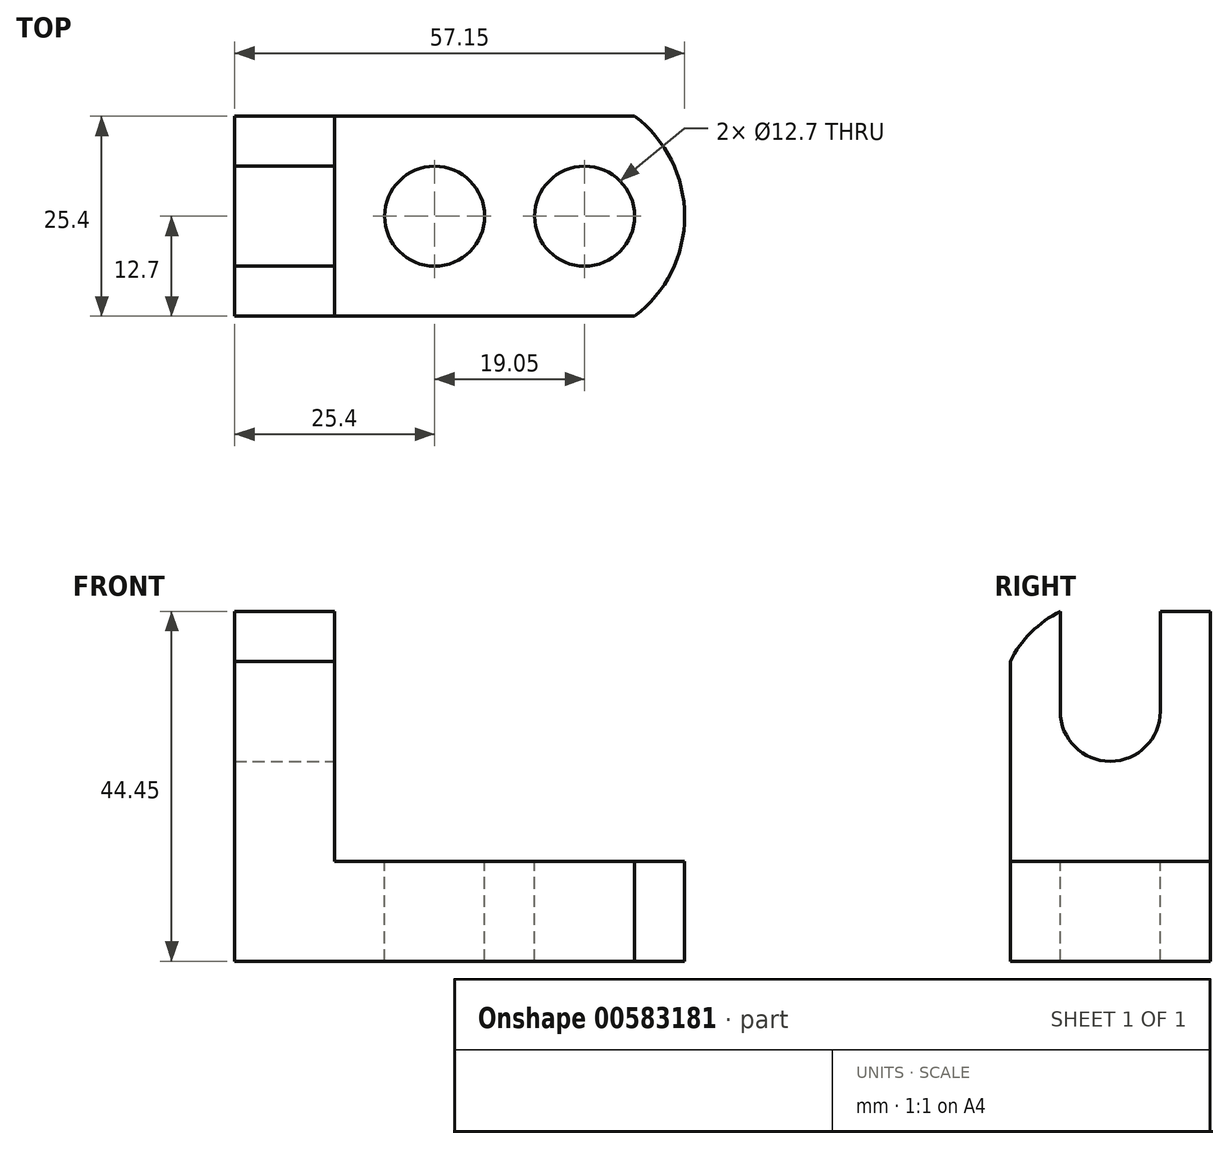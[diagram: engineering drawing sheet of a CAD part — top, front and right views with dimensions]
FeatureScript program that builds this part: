
annotation { "Feature Type Name" : "Feature", "Feature Type Description" : "" }
export const myFeature = defineFeature(function(context is Context, id is Id, definition is map)
    precondition{}
    {
        {
            var Q0;
            Q0=qCreatedBy(makeId("Front.planeOp"),FACE);
            var sketch = newSketch(context, id + "F0", { "sketchPlane" : qUnion([Q0])});
            skLineSegment(sketch, "E0.bottom", {"start": v(0, 0) * mm, "end": v(-57.15, 0) * mm});
            skLineSegment(sketch, "E0.top", {"start": v(0, 44.45) * mm, "end": v(-57.15, 44.45) * mm});
            skLineSegment(sketch, "E0.left", {"start": v(0, 0) * mm, "end": v(0, 44.45) * mm});
            skLineSegment(sketch, "E0.right", {"start": v(-57.15, 0) * mm, "end": v(-57.15, 44.45) * mm});
            skSolve(sketch);
        }
        {
            var Q0;
            Q0=makeQuery(id+"F0.imprint","IMPRINT",FACE,{"disambiguationData":[TD([[makeQuery(id+"F0.imprint","IMPRINT",EDGE,{"derivedFrom":sQuery(id+"F0.wireOp",EDGE,"E0.bottom")}),-1.0]])]});
            extrude(context, id + "F1", {"entities" : qUnion([Q0]), "depth" : 25.4 * mm, "offsetDistance" : 25.4 * mm});
        }
        {
            var Q0;
            Q0=makeQuery(id+"F1.opExtrude","CAP_FACE",FACE,{"disambiguationData":[OSD([sQuery(id+"F0.wireOp",EDGE,"E0.bottom"),sQuery(id+"F0.wireOp",EDGE,"E0.top"),sQuery(id+"F0.wireOp",EDGE,"E0.left"),sQuery(id+"F0.wireOp",EDGE,"E0.right")])],"isStart":false});
            var sketch = newSketch(context, id + "F2", { "sketchPlane" : qUnion([Q0])});
            skLineSegment(sketch, "E1", {"start": v(-57.15, 44.45) * mm, "end": v(-44.45, 44.45) * mm});
            skLineSegment(sketch, "E2", {"start": v(-44.45, 44.45) * mm, "end": v(-44.45, 12.7) * mm});
            skLineSegment(sketch, "E3", {"start": v(-44.45, 12.7) * mm, "end": v(0, 12.7) * mm});
            skSolve(sketch);
        }
        {
            var Q0;
            {var subQ0=sQuery(id+"F2.wireOp",EDGE,"E2");Q0=makeQuery(id+"F2.imprint","IMPRINT",FACE,{"disambiguationData":[TD([[makeQuery(id+"F2.imprint","IMPRINT",EDGE,{"derivedFrom":subQ0}),1.0]])]});}
            extrude(context, id + "F3", {"entities" : qUnion([Q0]), "operationType" : NewBodyOperationType.REMOVE, "endBound" : BoundingType.THROUGH_ALL, "oppositeDirection" : true, "depth" : 25.4 * mm, "offsetDistance" : 25.4 * mm});
        }
        {
            var Q0;
            Q0=makeQuery(id+"F3.boolean.opBoolean","COPY",FACE,{"derivedFrom":makeQuery(id+"F3.opExtrude","SWEPT_FACE",FACE,{"disambiguationData":[OSD([sQuery(id+"F2.wireOp",EDGE,"E3")])]})});
            var sketch = newSketch(context, id + "F4", { "sketchPlane" : qUnion([Q0])});
            skLineSegment(sketch, "E4", {"start": v(0, 0) * mm, "end": v(-6.35, 0) * mm});
            skArc(sketch, "E5", {"start": v(-6.35, -25.4) * mm, "mid": v(0, -12.7) * mm, "end": v(-6.35, 0) * mm});
            skSolve(sketch);
        }
        {
            var Q0;
            {var subQ0=sQuery(id+"F4.wireOp",EDGE,"E4");Q0=makeQuery(id+"F4.imprint","IMPRINT",FACE,{"disambiguationData":[TD([[makeQuery(id+"F4.imprint","IMPRINT",EDGE,{"derivedFrom":subQ0}),-1.0]])]});}
            var Q1;
            {var subQ0=sQuery(id+"F4.wireOp",EDGE,"E5");var subQ1=sQuery(id+"F2.wireOp",EDGE,"E3");var subQ2=makeQuery(id+"F3.boolean.opBoolean","COPY",EDGE,{"derivedFrom":makeQuery(id+"F3.opExtrude","CAP_EDGE",EDGE,{"disambiguationData":[OSD([subQ1])],"isStart":true})});var subQ3=makeQuery(id+"F4.imprint","INTERSECT",VERTEX,{"derivedFrom":[subQ2,subQ0]});Q1=makeQuery(id+"F4.imprint","IMPRINT",FACE,{"disambiguationData":[TD([[makeQuery(id+"F4.imprint","IMPRINT",EDGE,{"disambiguationData":[TD([[subQ3,-1.0]])],"derivedFrom":subQ0}),-1.0]])]});}
            extrude(context, id + "F5", {"entities" : qUnion([Q0, Q1]), "operationType" : NewBodyOperationType.REMOVE, "endBound" : BoundingType.THROUGH_ALL, "oppositeDirection" : true, "depth" : 25.4 * mm, "offsetDistance" : 25.4 * mm});
        }
        {
            var Q0;
            Q0=makeQuery(id+"F3.boolean.opBoolean","COPY",FACE,{"derivedFrom":makeQuery(id+"F3.opExtrude","SWEPT_FACE",FACE,{"disambiguationData":[OSD([sQuery(id+"F2.wireOp",EDGE,"E3")])]})});
            var sketch = newSketch(context, id + "F6", { "sketchPlane" : qUnion([Q0])});
            skPoint(sketch, "E6.endSnap0", {"position": v(0, -12.7) * mm});
            skCircle(sketch, "E7", {"center": v(-12.7, -12.7) * mm, "radius": 6.35 * mm});
            skCircle(sketch, "E8", {"center": v(-31.75, -12.7) * mm, "radius": 6.35 * mm});
            skSolve(sketch);
        }
        {
            var Q0;
            Q0=makeQuery(id+"F6.imprint","IMPRINT",FACE,{"disambiguationData":[TD([[makeQuery(id+"F6.imprint","IMPRINT",EDGE,{"derivedFrom":sQuery(id+"F6.wireOp",EDGE,"E8")}),1.0]])]});
            var Q1;
            Q1=makeQuery(id+"F6.imprint","IMPRINT",FACE,{"disambiguationData":[TD([[makeQuery(id+"F6.imprint","IMPRINT",EDGE,{"derivedFrom":sQuery(id+"F6.wireOp",EDGE,"E7")}),1.0]])]});
            extrude(context, id + "F7", {"entities" : qUnion([Q0, Q1]), "operationType" : NewBodyOperationType.REMOVE, "endBound" : BoundingType.THROUGH_ALL, "oppositeDirection" : true, "depth" : 25.4 * mm, "offsetDistance" : 25.4 * mm});
        }
        {
            var Q0;
            Q0=makeQuery(id+"F3.boolean.opBoolean","COPY",FACE,{"derivedFrom":makeQuery(id+"F3.opExtrude","SWEPT_FACE",FACE,{"disambiguationData":[OSD([sQuery(id+"F2.wireOp",EDGE,"E2")])]})});
            var sketch = newSketch(context, id + "F8", { "sketchPlane" : qUnion([Q0])});
            skCircle(sketch, "E9", {"center": v(-12.7, 31.75) * mm, "radius": 6.35 * mm});
            skLineSegment(sketch, "E10", {"start": v(-6.35, 31.75) * mm, "end": v(-6.35, 44.45) * mm});
            skLineSegment(sketch, "E11", {"start": v(-19.05, 31.75) * mm, "end": v(-19.05, 44.45) * mm});
            skSolve(sketch);
        }
        {
            var Q0;
            {var subQ0=sQuery(id+"F8.wireOp",EDGE,"E10");Q0=makeQuery(id+"F8.imprint","IMPRINT",FACE,{"disambiguationData":[TD([[makeQuery(id+"F8.imprint","IMPRINT",EDGE,{"derivedFrom":subQ0}),1.0]])]});}
            var Q1;
            {var subQ0=sQuery(id+"F8.wireOp",EDGE,"E9");var subQ1=makeQuery(id+"F8.imprint","INTERSECT",VERTEX,{"derivedFrom":[subQ0,sQuery(id+"F8.wireOp",EDGE,"E10")]});Q1=makeQuery(id+"F8.imprint","IMPRINT",FACE,{"disambiguationData":[TD([[makeQuery(id+"F8.imprint","IMPRINT",EDGE,{"disambiguationData":[TD([[subQ1,-1.0]])],"derivedFrom":subQ0}),1.0]])]});}
            extrude(context, id + "F9", {"entities" : qUnion([Q0, Q1]), "operationType" : NewBodyOperationType.REMOVE, "endBound" : BoundingType.THROUGH_ALL, "oppositeDirection" : true, "depth" : 25.4 * mm, "offsetDistance" : 25.4 * mm});
        }
        {
            var Q0;
            Q0=makeQuery(id+"F3.boolean.opBoolean","COPY",FACE,{"derivedFrom":makeQuery(id+"F3.opExtrude","SWEPT_FACE",FACE,{"disambiguationData":[OSD([sQuery(id+"F2.wireOp",EDGE,"E2")])]})});
            var sketch = newSketch(context, id + "F10", { "sketchPlane" : qUnion([Q0])});
            skLineSegment(sketch, "E12", {"start": v(-25.4, 44.45) * mm, "end": v(-25.4, 38.1) * mm});
            skArc(sketch, "E13", {"start": v(0, 38.1) * mm, "mid": v(-12.7, 45.95) * mm, "end": v(-25.4, 38.1) * mm});
            skPoint(sketch, "E13.startSnap0", {"position": v(-6.35, 38.1) * mm});
            skSolve(sketch);
        }
        {
            var Q0;
            {var subQ0=sQuery(id+"F10.wireOp",EDGE,"E12");Q0=makeQuery(id+"F10.imprint","IMPRINT",FACE,{"disambiguationData":[TD([[makeQuery(id+"F10.imprint","IMPRINT",EDGE,{"derivedFrom":subQ0}),1.0]])]});}
            var Q1;
            {var subQ1=sQuery(id+"F0.wireOp",EDGE,"E0.top");var subQ3=sQuery(id+"F8.wireOp",EDGE,"E10");var subQ4=sQuery(id+"F2.wireOp",EDGE,"E2");var subQ6=makeQuery(id+"F9.boolean.opBoolean","SPLIT",EDGE,{"disambiguationData":[TD([makeQuery(id+"F9.opExtrude","SWEPT_FACE",FACE,{"disambiguationData":[OSD([subQ3])]})])],"derivedFrom":makeQuery(id+"F3.boolean.opBoolean","COPY",EDGE,{"derivedFrom":makeQuery(id+"F3.opExtrude","SWEPT_EDGE",EDGE,{"disambiguationData":[OSD([subQ1,sQuery(id+"F2.wireOp",EDGE,"E1"),subQ4])]})})});Q1=makeQuery(id+"F10.imprint","IMPRINT",FACE,{"disambiguationData":[TD([[makeQuery(id+"F10.imprint","IMPRINT",EDGE,{"derivedFrom":subQ6}),1.0]])]});}
            extrude(context, id + "F11", {"entities" : qUnion([Q0, Q1]), "operationType" : NewBodyOperationType.REMOVE, "endBound" : BoundingType.THROUGH_ALL, "oppositeDirection" : true, "depth" : 25.4 * mm, "offsetDistance" : 25.4 * mm});
        }
    });
